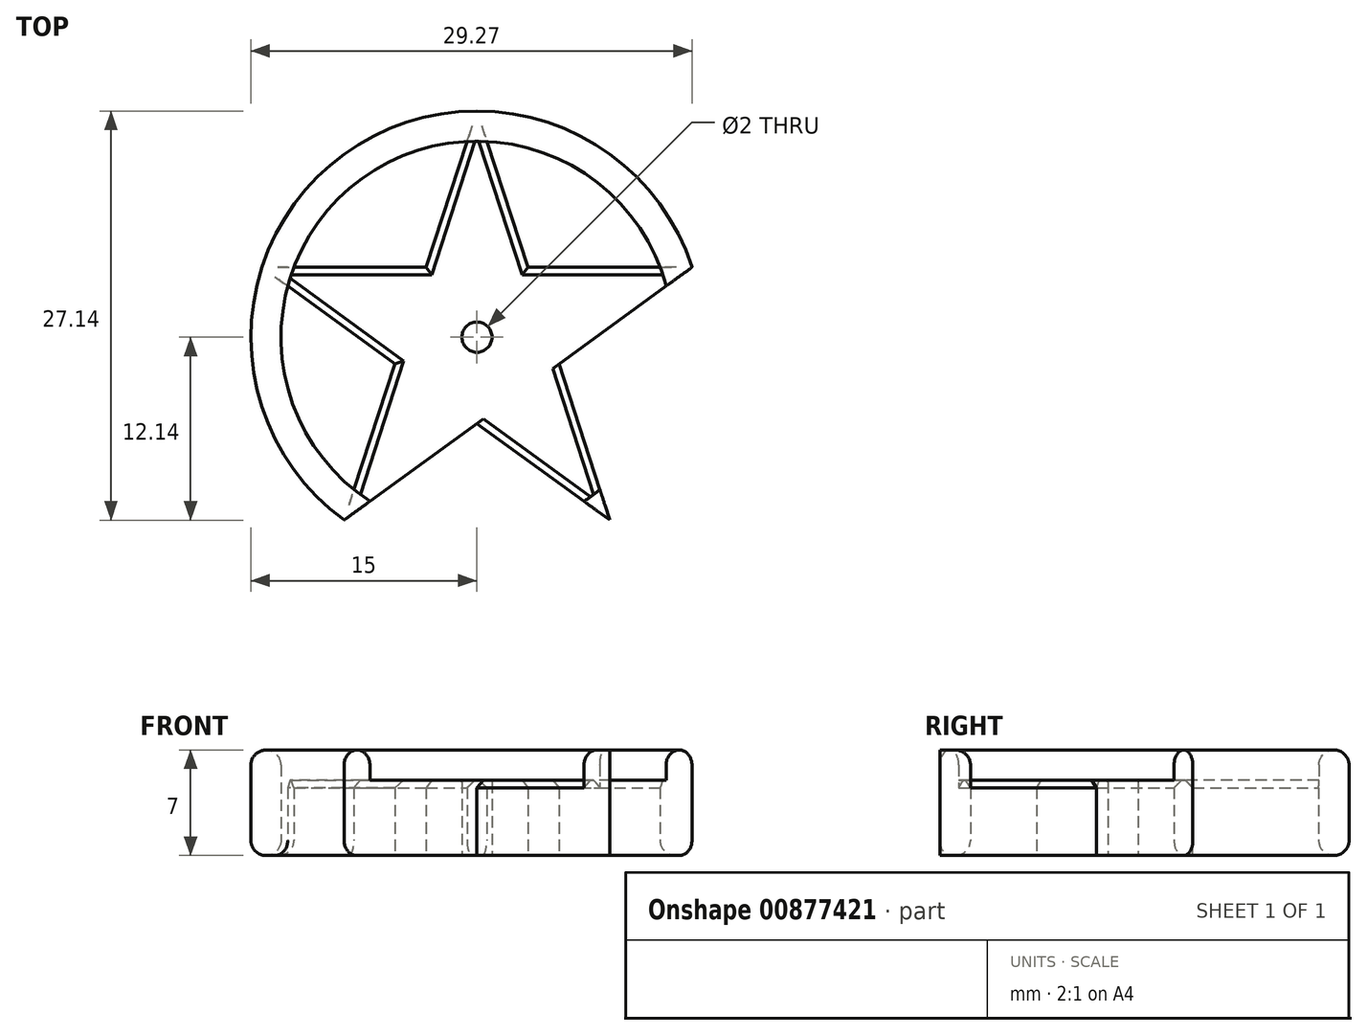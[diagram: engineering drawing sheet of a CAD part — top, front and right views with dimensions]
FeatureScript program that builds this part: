
annotation { "Feature Type Name" : "Feature", "Feature Type Description" : "" }
export const myFeature = defineFeature(function(context is Context, id is Id, definition is map)
    precondition{}
    {
        {
            var Q0;
            Q0=qCreatedBy(makeId("Top.planeOp"),FACE);
            var sketch = newSketch(context, id + "F0", { "sketchPlane" : qUnion([Q0])});
            skCircle(sketch, "E0", {"center": v(0, 0) * mm, "radius": 1 * mm});
            skCircle(sketch, "E1", {"center": v(0, 0) * mm, "radius": 15 * mm});
            skCircle(sketch, "E2", {"center": v(0, 0) * mm, "radius": 13 * mm});
            skCircle(sketch, "E3.cCircle", {"center": v(0, 0) * mm, "radius": 15 * mm, "construction": true});
            skLineSegment(sketch, "E4", {"start": v(0, 15) * mm, "end": v(-8.82, -12.14) * mm});
            skLineSegment(sketch, "E5", {"start": v(-8.82, -12.14) * mm, "end": v(14.27, 4.64) * mm});
            skLineSegment(sketch, "E6", {"start": v(14.27, 4.64) * mm, "end": v(-14.27, 4.64) * mm});
            skLineSegment(sketch, "E7", {"start": v(-14.27, 4.64) * mm, "end": v(8.82, -12.14) * mm});
            skLineSegment(sketch, "E8", {"start": v(8.82, -12.14) * mm, "end": v(0, 15) * mm});
            skSolve(sketch);
        }
        {
            var Q0;
            {var subQ0=sQuery(id+"F0.wireOp",EDGE,"E4");var subQ5=sQuery(id+"F0.wireOp",EDGE,"E2");var subQ6=makeQuery(id+"F0.imprint","INTERSECT",VERTEX,{"disambiguationData":[OD(0.0)],"derivedFrom":[subQ5,subQ0]});Q0=makeQuery(id+"F0.imprint","IMPRINT",FACE,{"disambiguationData":[TD([[makeQuery(id+"F0.imprint","IMPRINT",EDGE,{"disambiguationData":[TD([[subQ6,-1.0]])],"derivedFrom":subQ5}),-1.0]])]});}
            var Q1;
            {var subQ0=sQuery(id+"F0.wireOp",EDGE,"E8");var subQ1=sQuery(id+"F0.wireOp",EDGE,"E2");var subQ2=makeQuery(id+"F0.imprint","INTERSECT",VERTEX,{"disambiguationData":[OD(0.0)],"derivedFrom":[subQ1,subQ0]});Q1=makeQuery(id+"F0.imprint","IMPRINT",FACE,{"disambiguationData":[TD([[makeQuery(id+"F0.imprint","IMPRINT",EDGE,{"disambiguationData":[TD([[subQ2,-1.0]])],"derivedFrom":subQ1}),-1.0]])]});}
            var Q2;
            {var subQ3=sQuery(id+"F0.wireOp",EDGE,"E6");var subQ5=sQuery(id+"F0.wireOp",EDGE,"E2");var subQ6=makeQuery(id+"F0.imprint","INTERSECT",VERTEX,{"disambiguationData":[OD(0.0)],"derivedFrom":[subQ5,subQ3]});Q2=makeQuery(id+"F0.imprint","IMPRINT",FACE,{"disambiguationData":[TD([[makeQuery(id+"F0.imprint","IMPRINT",EDGE,{"disambiguationData":[TD([[subQ6,-1.0]])],"derivedFrom":subQ5}),-1.0]])]});}
            var Q3;
            {var subQ0=sQuery(id+"F0.wireOp",EDGE,"E6");var subQ1=sQuery(id+"F0.wireOp",EDGE,"E2");var subQ2=makeQuery(id+"F0.imprint","INTERSECT",VERTEX,{"disambiguationData":[OD(0.0)],"derivedFrom":[subQ1,subQ0]});Q3=makeQuery(id+"F0.imprint","IMPRINT",FACE,{"disambiguationData":[TD([[makeQuery(id+"F0.imprint","IMPRINT",EDGE,{"disambiguationData":[TD([[subQ2,1.0]])],"derivedFrom":subQ1}),-1.0]])]});}
            var Q4;
            {var subQ0=sQuery(id+"F0.wireOp",EDGE,"E5");var subQ5=sQuery(id+"F0.wireOp",EDGE,"E2");var subQ6=makeQuery(id+"F0.imprint","INTERSECT",VERTEX,{"disambiguationData":[OD(0.0)],"derivedFrom":[subQ5,subQ0]});Q4=makeQuery(id+"F0.imprint","IMPRINT",FACE,{"disambiguationData":[TD([[makeQuery(id+"F0.imprint","IMPRINT",EDGE,{"disambiguationData":[TD([[subQ6,1.0]])],"derivedFrom":subQ5}),-1.0]])]});}
            var Q5;
            {var subQ0=sQuery(id+"F0.wireOp",EDGE,"E7");var subQ1=sQuery(id+"F0.wireOp",EDGE,"E2");var subQ2=makeQuery(id+"F0.imprint","INTERSECT",VERTEX,{"disambiguationData":[OD(1.0)],"derivedFrom":[subQ1,subQ0]});Q5=makeQuery(id+"F0.imprint","IMPRINT",FACE,{"disambiguationData":[TD([[makeQuery(id+"F0.imprint","IMPRINT",EDGE,{"disambiguationData":[TD([[subQ2,-1.0]])],"derivedFrom":subQ1}),-1.0]])]});}
            var Q6;
            {var subQ0=sQuery(id+"F0.wireOp",EDGE,"E5");var subQ5=sQuery(id+"F0.wireOp",EDGE,"E2");var subQ6=makeQuery(id+"F0.imprint","INTERSECT",VERTEX,{"disambiguationData":[OD(1.0)],"derivedFrom":[subQ5,subQ0]});Q6=makeQuery(id+"F0.imprint","IMPRINT",FACE,{"disambiguationData":[TD([[makeQuery(id+"F0.imprint","IMPRINT",EDGE,{"disambiguationData":[TD([[subQ6,-1.0]])],"derivedFrom":subQ5}),-1.0]])]});}
            var Q7;
            {var subQ0=sQuery(id+"F0.wireOp",EDGE,"E4");var subQ1=sQuery(id+"F0.wireOp",EDGE,"E2");var subQ2=makeQuery(id+"F0.imprint","INTERSECT",VERTEX,{"disambiguationData":[OD(1.0)],"derivedFrom":[subQ1,subQ0]});Q7=makeQuery(id+"F0.imprint","IMPRINT",FACE,{"disambiguationData":[TD([[makeQuery(id+"F0.imprint","IMPRINT",EDGE,{"disambiguationData":[TD([[subQ2,-1.0]])],"derivedFrom":subQ1}),-1.0]])]});}
            var Q8;
            {var subQ3=sQuery(id+"F0.wireOp",EDGE,"E7");var subQ5=sQuery(id+"F0.wireOp",EDGE,"E2");var subQ6=makeQuery(id+"F0.imprint","INTERSECT",VERTEX,{"disambiguationData":[OD(0.0)],"derivedFrom":[subQ5,subQ3]});Q8=makeQuery(id+"F0.imprint","IMPRINT",FACE,{"disambiguationData":[TD([[makeQuery(id+"F0.imprint","IMPRINT",EDGE,{"disambiguationData":[TD([[subQ6,-1.0]])],"derivedFrom":subQ5}),-1.0]])]});}
            var Q9;
            {var subQ0=sQuery(id+"F0.wireOp",EDGE,"E6");var subQ1=sQuery(id+"F0.wireOp",EDGE,"E2");var subQ2=makeQuery(id+"F0.imprint","INTERSECT",VERTEX,{"disambiguationData":[OD(1.0)],"derivedFrom":[subQ1,subQ0]});Q9=makeQuery(id+"F0.imprint","IMPRINT",FACE,{"disambiguationData":[TD([[makeQuery(id+"F0.imprint","IMPRINT",EDGE,{"disambiguationData":[TD([[subQ2,-1.0]])],"derivedFrom":subQ1}),-1.0]])]});}
            extrude(context, id + "F1", {"entities" : qUnion([Q0, Q1, Q2, Q3, Q4, Q5, Q6, Q7, Q8, Q9]), "depth" : 7 * mm, "offsetDistance" : 25 * mm});
        }
        {
            var Q0;
            {var subQ0=sQuery(id+"F0.wireOp",EDGE,"E8");var subQ1=sQuery(id+"F0.wireOp",EDGE,"E2");var subQ2=makeQuery(id+"F0.imprint","INTERSECT",VERTEX,{"disambiguationData":[OD(0.0)],"derivedFrom":[subQ1,subQ0]});Q0=makeQuery(id+"F0.imprint","IMPRINT",FACE,{"disambiguationData":[TD([[makeQuery(id+"F0.imprint","IMPRINT",EDGE,{"disambiguationData":[TD([[subQ2,-1.0]])],"derivedFrom":subQ1}),1.0]])]});}
            var Q1;
            Q1=makeQuery(id+"F0.imprint","IMPRINT",FACE,{"disambiguationData":[TD([[makeQuery(id+"F0.imprint","IMPRINT",EDGE,{"derivedFrom":sQuery(id+"F0.wireOp",EDGE,"E0")}),-1.0]])]});
            var Q2;
            {var subQ0=sQuery(id+"F0.wireOp",EDGE,"E6");var subQ1=sQuery(id+"F0.wireOp",EDGE,"E2");var subQ2=makeQuery(id+"F0.imprint","INTERSECT",VERTEX,{"disambiguationData":[OD(0.0)],"derivedFrom":[subQ1,subQ0]});Q2=makeQuery(id+"F0.imprint","IMPRINT",FACE,{"disambiguationData":[TD([[makeQuery(id+"F0.imprint","IMPRINT",EDGE,{"disambiguationData":[TD([[subQ2,1.0]])],"derivedFrom":subQ1}),1.0]])]});}
            var Q3;
            {var subQ0=sQuery(id+"F0.wireOp",EDGE,"E7");var subQ1=sQuery(id+"F0.wireOp",EDGE,"E2");var subQ2=makeQuery(id+"F0.imprint","INTERSECT",VERTEX,{"disambiguationData":[OD(1.0)],"derivedFrom":[subQ1,subQ0]});Q3=makeQuery(id+"F0.imprint","IMPRINT",FACE,{"disambiguationData":[TD([[makeQuery(id+"F0.imprint","IMPRINT",EDGE,{"disambiguationData":[TD([[subQ2,-1.0]])],"derivedFrom":subQ1}),1.0]])]});}
            var Q4;
            {var subQ0=sQuery(id+"F0.wireOp",EDGE,"E4");var subQ1=sQuery(id+"F0.wireOp",EDGE,"E2");var subQ2=makeQuery(id+"F0.imprint","INTERSECT",VERTEX,{"disambiguationData":[OD(1.0)],"derivedFrom":[subQ1,subQ0]});Q4=makeQuery(id+"F0.imprint","IMPRINT",FACE,{"disambiguationData":[TD([[makeQuery(id+"F0.imprint","IMPRINT",EDGE,{"disambiguationData":[TD([[subQ2,-1.0]])],"derivedFrom":subQ1}),1.0]])]});}
            var Q5;
            {var subQ0=sQuery(id+"F0.wireOp",EDGE,"E6");var subQ1=sQuery(id+"F0.wireOp",EDGE,"E2");var subQ2=makeQuery(id+"F0.imprint","INTERSECT",VERTEX,{"disambiguationData":[OD(1.0)],"derivedFrom":[subQ1,subQ0]});Q5=makeQuery(id+"F0.imprint","IMPRINT",FACE,{"disambiguationData":[TD([[makeQuery(id+"F0.imprint","IMPRINT",EDGE,{"disambiguationData":[TD([[subQ2,-1.0]])],"derivedFrom":subQ1}),1.0]])]});}
            extrude(context, id + "F2", {"entities" : qUnion([Q0, Q1, Q2, Q3, Q4, Q5]), "operationType" : NewBodyOperationType.ADD, "depth" : 5 * mm, "offsetDistance" : 25 * mm});
        }
        {
            var Q0;
            Q0=makeQuery(id+"F1.opExtrude","CAP_EDGE",EDGE,{"disambiguationData":[OSD([sQuery(id+"F0.wireOp",EDGE,"E1")])],"isStart":false});
            var Q1;
            Q1=makeQuery(id+"F1.opExtrude","CAP_EDGE",EDGE,{"disambiguationData":[OSD([sQuery(id+"F0.wireOp",EDGE,"E2")])],"isStart":false});
            var Q2;
            Q2=makeQuery(id+"F1.opExtrude","CAP_EDGE",EDGE,{"disambiguationData":[OSD([sQuery(id+"F0.wireOp",EDGE,"E1")])],"isStart":true});
            var Q3;
            {var subQ1=sQuery(id+"F0.wireOp",EDGE,"E5");var subQ2=sQuery(id+"F0.wireOp",EDGE,"E2");Q3=makeQuery(id+"F2.boolean.opBoolean","SPLIT",EDGE,{"disambiguationData":[TD([makeQuery(id+"F2.opExtrude","SWEPT_FACE",FACE,{"disambiguationData":[OSD([subQ1]),TDD([makeQuery(id+"F0.imprint","IMPRINT",EDGE,{"disambiguationData":[TD([[makeQuery(id+"F0.imprint","INTERSECT",VERTEX,{"disambiguationData":[OD(1.0)],"derivedFrom":[subQ2,subQ1]}),-1.0]])],"derivedFrom":subQ1})])]})])],"derivedFrom":makeQuery(id+"F1.opExtrude","CAP_EDGE",EDGE,{"disambiguationData":[OSD([subQ2])],"isStart":true})});}
            var Q4;
            {var subQ0=sQuery(id+"F0.wireOp",EDGE,"E5");var subQ1=sQuery(id+"F0.wireOp",EDGE,"E2");Q4=makeQuery(id+"F2.boolean.opBoolean","SPLIT",EDGE,{"disambiguationData":[TD([makeQuery(id+"F2.opExtrude","SWEPT_FACE",FACE,{"disambiguationData":[OSD([subQ0]),TDD([makeQuery(id+"F0.imprint","IMPRINT",EDGE,{"disambiguationData":[TD([[makeQuery(id+"F0.imprint","INTERSECT",VERTEX,{"disambiguationData":[OD(0.0)],"derivedFrom":[subQ1,subQ0]}),1.0]])],"derivedFrom":subQ0})])]})])],"derivedFrom":makeQuery(id+"F1.opExtrude","CAP_EDGE",EDGE,{"disambiguationData":[OSD([subQ1])],"isStart":true})});}
            var Q5;
            {var subQ1=sQuery(id+"F0.wireOp",EDGE,"E6");var subQ2=sQuery(id+"F0.wireOp",EDGE,"E2");Q5=makeQuery(id+"F2.boolean.opBoolean","SPLIT",EDGE,{"disambiguationData":[TD([makeQuery(id+"F2.opExtrude","SWEPT_FACE",FACE,{"disambiguationData":[OSD([subQ1]),TDD([makeQuery(id+"F0.imprint","IMPRINT",EDGE,{"disambiguationData":[TD([[makeQuery(id+"F0.imprint","INTERSECT",VERTEX,{"disambiguationData":[OD(0.0)],"derivedFrom":[subQ2,subQ1]}),-1.0]])],"derivedFrom":subQ1})])]})])],"derivedFrom":makeQuery(id+"F1.opExtrude","CAP_EDGE",EDGE,{"disambiguationData":[OSD([subQ2])],"isStart":true})});}
            var Q6;
            {var subQ0=sQuery(id+"F0.wireOp",EDGE,"E4");var subQ1=sQuery(id+"F0.wireOp",EDGE,"E2");Q6=makeQuery(id+"F2.boolean.opBoolean","SPLIT",EDGE,{"disambiguationData":[TD([makeQuery(id+"F2.opExtrude","SWEPT_FACE",FACE,{"disambiguationData":[OSD([subQ0]),TDD([makeQuery(id+"F0.imprint","IMPRINT",EDGE,{"disambiguationData":[TD([[makeQuery(id+"F0.imprint","INTERSECT",VERTEX,{"disambiguationData":[OD(0.0)],"derivedFrom":[subQ1,subQ0]}),-1.0]])],"derivedFrom":subQ0})])]})])],"derivedFrom":makeQuery(id+"F1.opExtrude","CAP_EDGE",EDGE,{"disambiguationData":[OSD([subQ1])],"isStart":true})});}
            var Q7;
            {var subQ0=sQuery(id+"F0.wireOp",EDGE,"E4");var subQ1=sQuery(id+"F0.wireOp",EDGE,"E2");Q7=makeQuery(id+"F2.boolean.opBoolean","SPLIT",EDGE,{"disambiguationData":[TD([makeQuery(id+"F2.opExtrude","SWEPT_FACE",FACE,{"disambiguationData":[OSD([subQ0]),TDD([makeQuery(id+"F0.imprint","IMPRINT",EDGE,{"disambiguationData":[TD([[makeQuery(id+"F0.imprint","INTERSECT",VERTEX,{"disambiguationData":[OD(1.0)],"derivedFrom":[subQ1,subQ0]}),1.0]])],"derivedFrom":subQ0})])]})])],"derivedFrom":makeQuery(id+"F1.opExtrude","CAP_EDGE",EDGE,{"disambiguationData":[OSD([subQ1])],"isStart":true})});}
            fillet(context, id + "F3", {"entities" : qUnion([Q0, Q1, Q2, Q3, Q4, Q5, Q6, Q7]), "radius" : 1 * mm, "tangentPropagation" : true, "allowEdgeOverflow" : false});
        }
        {
            var Q0;
            {var subQ0=sQuery(id+"F0.wireOp",EDGE,"E8");Q0=makeQuery(id+"F2.opExtrude","CAP_EDGE",EDGE,{"disambiguationData":[OSD([subQ0]),TDD([makeQuery(id+"F0.imprint","IMPRINT",EDGE,{"disambiguationData":[TD([[makeQuery(id+"F0.imprint","INTERSECT",VERTEX,{"disambiguationData":[OD(0.0)],"derivedFrom":[sQuery(id+"F0.wireOp",EDGE,"E2"),subQ0]}),1.0]])],"derivedFrom":subQ0})])],"isStart":false});}
            var Q1;
            {var subQ0=sQuery(id+"F0.wireOp",EDGE,"E6");Q1=makeQuery(id+"F2.opExtrude","CAP_EDGE",EDGE,{"disambiguationData":[OSD([subQ0]),TDD([makeQuery(id+"F0.imprint","IMPRINT",EDGE,{"disambiguationData":[TD([[makeQuery(id+"F0.imprint","INTERSECT",VERTEX,{"disambiguationData":[OD(0.0)],"derivedFrom":[sQuery(id+"F0.wireOp",EDGE,"E2"),subQ0]}),-1.0]])],"derivedFrom":subQ0})])],"isStart":false});}
            var Q2;
            {var subQ0=sQuery(id+"F0.wireOp",EDGE,"E5");Q2=makeQuery(id+"F2.opExtrude","CAP_EDGE",EDGE,{"disambiguationData":[OSD([subQ0]),TDD([makeQuery(id+"F0.imprint","IMPRINT",EDGE,{"disambiguationData":[TD([[makeQuery(id+"F0.imprint","INTERSECT",VERTEX,{"disambiguationData":[OD(0.0)],"derivedFrom":[sQuery(id+"F0.wireOp",EDGE,"E2"),subQ0]}),1.0]])],"derivedFrom":subQ0})])],"isStart":false});}
            var Q3;
            {var subQ0=sQuery(id+"F0.wireOp",EDGE,"E8");Q3=makeQuery(id+"F2.opExtrude","CAP_EDGE",EDGE,{"disambiguationData":[OSD([subQ0]),TDD([makeQuery(id+"F0.imprint","IMPRINT",EDGE,{"disambiguationData":[TD([[makeQuery(id+"F0.imprint","INTERSECT",VERTEX,{"disambiguationData":[OD(1.0)],"derivedFrom":[sQuery(id+"F0.wireOp",EDGE,"E2"),subQ0]}),-1.0]])],"derivedFrom":subQ0})])],"isStart":false});}
            var Q4;
            {var subQ0=sQuery(id+"F0.wireOp",EDGE,"E7");Q4=makeQuery(id+"F2.opExtrude","CAP_EDGE",EDGE,{"disambiguationData":[OSD([subQ0]),TDD([makeQuery(id+"F0.imprint","IMPRINT",EDGE,{"disambiguationData":[TD([[makeQuery(id+"F0.imprint","INTERSECT",VERTEX,{"disambiguationData":[OD(1.0)],"derivedFrom":[sQuery(id+"F0.wireOp",EDGE,"E2"),subQ0]}),1.0]])],"derivedFrom":subQ0})])],"isStart":false});}
            var Q5;
            {var subQ0=sQuery(id+"F0.wireOp",EDGE,"E5");Q5=makeQuery(id+"F2.opExtrude","CAP_EDGE",EDGE,{"disambiguationData":[OSD([subQ0]),TDD([makeQuery(id+"F0.imprint","IMPRINT",EDGE,{"disambiguationData":[TD([[makeQuery(id+"F0.imprint","INTERSECT",VERTEX,{"disambiguationData":[OD(1.0)],"derivedFrom":[sQuery(id+"F0.wireOp",EDGE,"E2"),subQ0]}),-1.0]])],"derivedFrom":subQ0})])],"isStart":false});}
            var Q6;
            {var subQ0=sQuery(id+"F0.wireOp",EDGE,"E4");Q6=makeQuery(id+"F2.opExtrude","CAP_EDGE",EDGE,{"disambiguationData":[OSD([subQ0]),TDD([makeQuery(id+"F0.imprint","IMPRINT",EDGE,{"disambiguationData":[TD([[makeQuery(id+"F0.imprint","INTERSECT",VERTEX,{"disambiguationData":[OD(1.0)],"derivedFrom":[sQuery(id+"F0.wireOp",EDGE,"E2"),subQ0]}),1.0]])],"derivedFrom":subQ0})])],"isStart":false});}
            var Q7;
            {var subQ0=sQuery(id+"F0.wireOp",EDGE,"E7");Q7=makeQuery(id+"F2.opExtrude","CAP_EDGE",EDGE,{"disambiguationData":[OSD([subQ0]),TDD([makeQuery(id+"F0.imprint","IMPRINT",EDGE,{"disambiguationData":[TD([[makeQuery(id+"F0.imprint","INTERSECT",VERTEX,{"disambiguationData":[OD(0.0)],"derivedFrom":[sQuery(id+"F0.wireOp",EDGE,"E2"),subQ0]}),-1.0]])],"derivedFrom":subQ0})])],"isStart":false});}
            var Q8;
            {var subQ0=sQuery(id+"F0.wireOp",EDGE,"E6");Q8=makeQuery(id+"F2.opExtrude","CAP_EDGE",EDGE,{"disambiguationData":[OSD([subQ0]),TDD([makeQuery(id+"F0.imprint","IMPRINT",EDGE,{"disambiguationData":[TD([[makeQuery(id+"F0.imprint","INTERSECT",VERTEX,{"disambiguationData":[OD(1.0)],"derivedFrom":[sQuery(id+"F0.wireOp",EDGE,"E2"),subQ0]}),1.0]])],"derivedFrom":subQ0})])],"isStart":false});}
            var Q9;
            {var subQ0=sQuery(id+"F0.wireOp",EDGE,"E4");Q9=makeQuery(id+"F2.opExtrude","CAP_EDGE",EDGE,{"disambiguationData":[OSD([subQ0]),TDD([makeQuery(id+"F0.imprint","IMPRINT",EDGE,{"disambiguationData":[TD([[makeQuery(id+"F0.imprint","INTERSECT",VERTEX,{"disambiguationData":[OD(0.0)],"derivedFrom":[sQuery(id+"F0.wireOp",EDGE,"E2"),subQ0]}),-1.0]])],"derivedFrom":subQ0})])],"isStart":false});}
            chamfer(context, id + "F4", {"entities" : qUnion([Q0, Q1, Q2, Q3, Q4, Q5, Q6, Q7, Q8, Q9]), "width" : .5 * mm, "tangentPropagation" : true});
        }
        {
            var Q0;
            Q0=makeQuery(id+"F2.opExtrude","CAP_EDGE",EDGE,{"disambiguationData":[OSD([sQuery(id+"F0.wireOp",EDGE,"E0")])],"isStart":false});
            fillet(context, id + "F5", {"entities" : qUnion([Q0]), "radius" : .1 * mm, "tangentPropagation" : true, "allowEdgeOverflow" : false});
        }
    });
